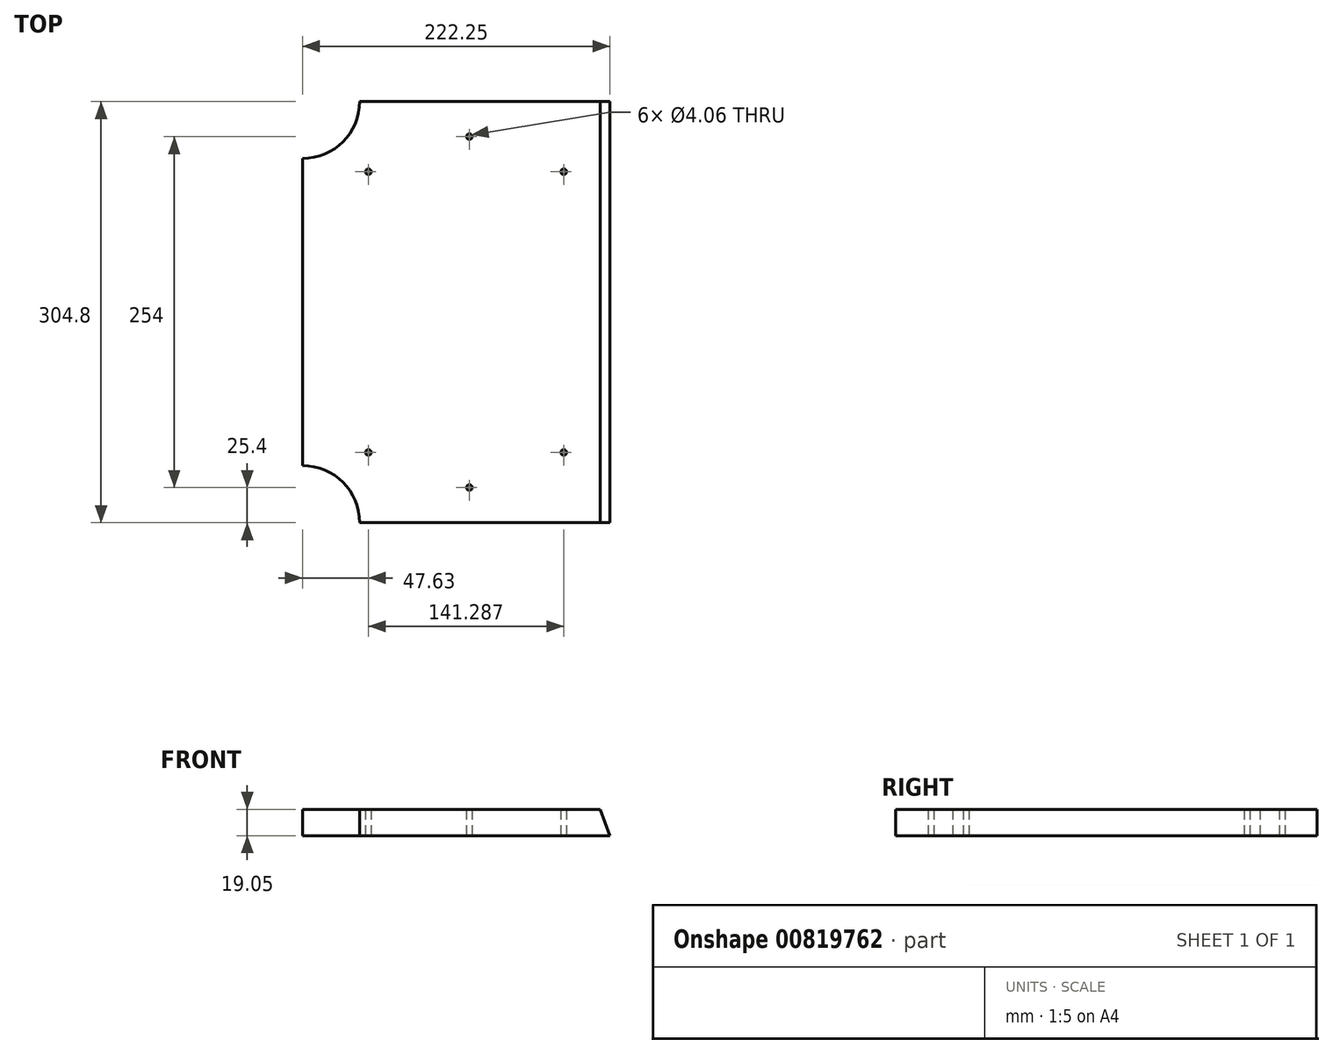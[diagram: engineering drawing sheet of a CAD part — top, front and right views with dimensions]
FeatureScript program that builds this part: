
annotation { "Feature Type Name" : "Feature", "Feature Type Description" : "" }
export const myFeature = defineFeature(function(context is Context, id is Id, definition is map)
    precondition{}
    {
        {
            var Q0;
            Q0=qCreatedBy(makeId("Top.planeOp"),FACE);
            var sketch = newSketch(context, id + "F0", { "sketchPlane" : qUnion([Q0])});
            skLineSegment(sketch, "E0.bottom", {"start": v(-69.85, 152.4) * mm, "end": v(111.13, 152.4) * mm});
            skLineSegment(sketch, "E0.top", {"start": v(-69.85, -152.4) * mm, "end": v(111.12, -152.4) * mm});
            skLineSegment(sketch, "E0.left", {"start": v(-111.13, 111.13) * mm, "end": v(-111.13, -111.12) * mm});
            skLineSegment(sketch, "E0.right", {"start": v(111.13, 152.4) * mm, "end": v(111.12, -152.4) * mm});
            skPoint(sketch, "E0.middle", {"position": v(0, 0) * mm});
            skArc(sketch, "E1", {"start": v(-69.85, -152.4) * mm, "mid": v(-81.94, -123.21) * mm, "end": v(-111.13, -111.12) * mm});
            skArc(sketch, "E2", {"start": v(-111.13, 111.13) * mm, "mid": v(-81.94, 123.21) * mm, "end": v(-69.85, 152.4) * mm});
            skLineSegment(sketch, "E3", {"start": v(77.79, 152.4) * mm, "end": v(77.79, -152.4) * mm, "construction": true});
            skLineSegment(sketch, "E4", {"start": v(-63.5, 152.4) * mm, "end": v(-63.5, -152.4) * mm, "construction": true});
            skLineSegment(sketch, "E5", {"start": v(-111.13, 101.6) * mm, "end": v(111.13, 101.6) * mm, "construction": true});
            skLineSegment(sketch, "E6", {"start": v(-111.13, -101.6) * mm, "end": v(111.13, -101.6) * mm, "construction": true});
            skLineSegment(sketch, "E7", {"start": v(-111.13, -127) * mm, "end": v(111.12, -127) * mm, "construction": true});
            skLineSegment(sketch, "E8", {"start": v(-111.12, 127) * mm, "end": v(111.13, 127) * mm, "construction": true});
            skLineSegment(sketch, "E9", {"start": v(9.53, 152.4) * mm, "end": v(9.52, -152.4) * mm, "construction": true});
            skPoint(sketch, "E9.endSnap0", {"position": v(20.64, -152.4) * mm});
            skCircle(sketch, "E10", {"center": v(-63.5, 101.6) * mm, "radius": 2.03 * mm});
            skCircle(sketch, "E11", {"center": v(77.79, 101.6) * mm, "radius": 2.03 * mm});
            skCircle(sketch, "E12", {"center": v(77.79, -101.6) * mm, "radius": 2.03 * mm});
            skCircle(sketch, "E13", {"center": v(-63.5, -101.6) * mm, "radius": 2.03 * mm});
            skCircle(sketch, "E14", {"center": v(9.52, -127) * mm, "radius": 2.03 * mm});
            skCircle(sketch, "E15", {"center": v(9.53, 127) * mm, "radius": 2.03 * mm});
            skSolve(sketch);
        }
        {
            var Q0;
            Q0=makeQuery(id+"F0.imprint","IMPRINT",FACE,{"disambiguationData":[TD([[makeQuery(id+"F0.imprint","IMPRINT",EDGE,{"derivedFrom":sQuery(id+"F0.wireOp",EDGE,"E0.bottom")}),-1.0]])]});
            extrude(context, id + "F1", {"entities" : qUnion([Q0]), "depth" : 19.05 * mm, "offsetDistance" : 25.4 * mm});
        }
        {
            var Q0;
            Q0=makeQuery(id+"F1.opExtrude","SWEPT_FACE",FACE,{"disambiguationData":[OSD([sQuery(id+"F0.wireOp",EDGE,"E0.top")])]});
            var sketch = newSketch(context, id + "F2", { "sketchPlane" : qUnion([Q0])});
            skLineSegment(sketch, "E16", {"start": v(111.12, 19.05) * mm, "end": v(111.12, 0) * mm});
            skLineSegment(sketch, "E17", {"start": v(111.12, 0) * mm, "end": v(104.2, 19.05) * mm});
            skLineSegment(sketch, "E18", {"start": v(104.2, 19.05) * mm, "end": v(111.12, 19.05) * mm});
            skSolve(sketch);
        }
        {
            var Q0;
            Q0 = qSketchRegion(id + "F2", true);
            extrude(context, id + "F3", {"entities" : qUnion([Q0]), "operationType" : NewBodyOperationType.REMOVE, "endBound" : BoundingType.UP_TO_NEXT, "oppositeDirection" : true, "depth" : 25.4 * mm, "offsetDistance" : 25.4 * mm});
        }
    });
